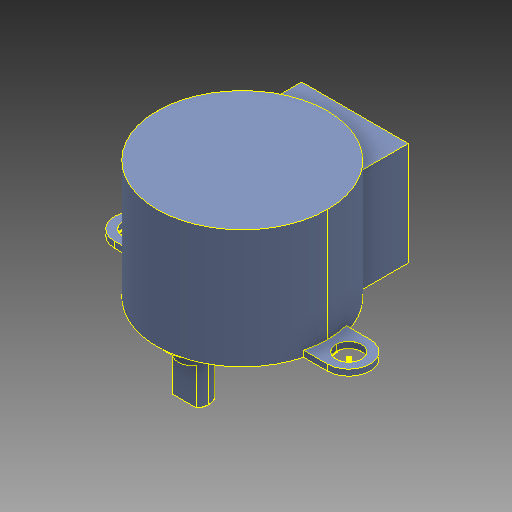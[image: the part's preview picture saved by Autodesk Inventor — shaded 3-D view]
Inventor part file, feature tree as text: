
AUTODESK INVENTOR PART (.ipt)
format: ipt  version: 2019 (Build 230136000, 136)  size: 206,848 bytes
history: native  units: mm
features: other x2, sketch x1
ambient origin geometry x8: Origin, YZ Plane, XZ Plane, XY Plane, X Axis, Y Axis, Z Axis, Center Point
bodies: Body1 (feature_tree), Body2 (feature_tree), Body3 (feature_tree), Body4 (feature_tree), Body5 (feature_tree), Body6 (feature_tree), Body7 (feature_tree), Body8 (feature_tree), Body9 (feature_tree), Body10 (feature_tree), Body11 (feature_tree), Body12 (feature_tree), Body13 (feature_tree), Body14 (feature_tree), Body15 (feature_tree), Body16 (feature_tree), Body17 (feature_tree), Body18 (feature_tree), Body19 (feature_tree), Body20 (feature_tree), Body21 (feature_tree), Body22 (feature_tree), Body23 (feature_tree), Body24 (feature_tree), Body25 (feature_tree), Body26 (feature_tree), Body27 (feature_tree), Body28 (feature_tree), Body29 (feature_tree), Body30 (feature_tree), Body31 (feature_tree)
feature tree (3):
  sketch  "Skizze1"
  other  "Zusammengesetzt1"
  other  "Fläche1"
